# Revit family: Shower-Shower_Trim-KOHLER-Tempered-K-TS22028_1
name_source: partatom
category: Plumbing Fixtures
units: mm (PartAtom-declared; Revit-internal decimal feet)

## family parameters
Cut with Voids When Loaded = No
Host = Face
OmniClass Number = 23.31.17.00
OmniClass Title = Showers
Part Type = Normal
Room Calculation Point = No
Round Connector Dimension = Use Diameter
Shared = No

## types (5) — shared parameters
ADA Compliant = No
Assembly Code = D2010700
CW Connection = No
Cold Water Inlet = Cold Water Inlet
Date Modified = 08/18/2022
Default Elevation = 42"
Description = Rite-Temp shower trim set, valve not included
Drain Included = No
Flow Rate = 2 GPM
HW Connection = Yes
Handle Clearance = 3 1/4"
Height = 6 1/4"
Hot Water Inlet = Tempered Water Inlet
Length = 6 13/16"
Manufacturer = Kohler Co.
Master Format 2014 = 22 42 23
Master Format 2014 Name = Residential Showers
Material = Premium Material Construction
Pressure = 80.00 psi
Product Documentation Link = https://www.us.kohler.com
Product Name = Tempered
Product Page URL = http://www.us.kohler.com
URL = https://www.us.kohler.com
Vent Connection = No
Waste Connection = No
Waste Water Outlet = Waste Water Outlet
WaterSense Certified = Yes
Width = 6 1/4"

## per-type parameters (varying)
| type | Finish | Model | Type |
| CP-Polished Chrome | Kohler-Metal-CP-Polished_Chrome | K-TS22028-4-CP | 1 |
| SN-Vibrant Polished Nickel | Kohler-Metal-SN-Vibrant_Polished_Nickel | K-TS22028-4-SN | 2 |
| BN-Vibrant Brushed Nickel | Kohler-Metal-BN-Vibrant_Brushed_Nickel | K-TS22028-4-BN | 3 |
| BL-Matte Black | Kohler-Metal-BL-Matte_Black | K-TS22028-4-BL | 4 |
| 2MB-Vibrant Brushed Moderne Brass | Kohler-Metal-2MB-Vibrant_Brushed_Moderne_Brass | K-TS22028-4-2MB | 5 |

## geometry (parser evidence)
native form markers: Sweep x7
no freeform markers — native parametric forms only
